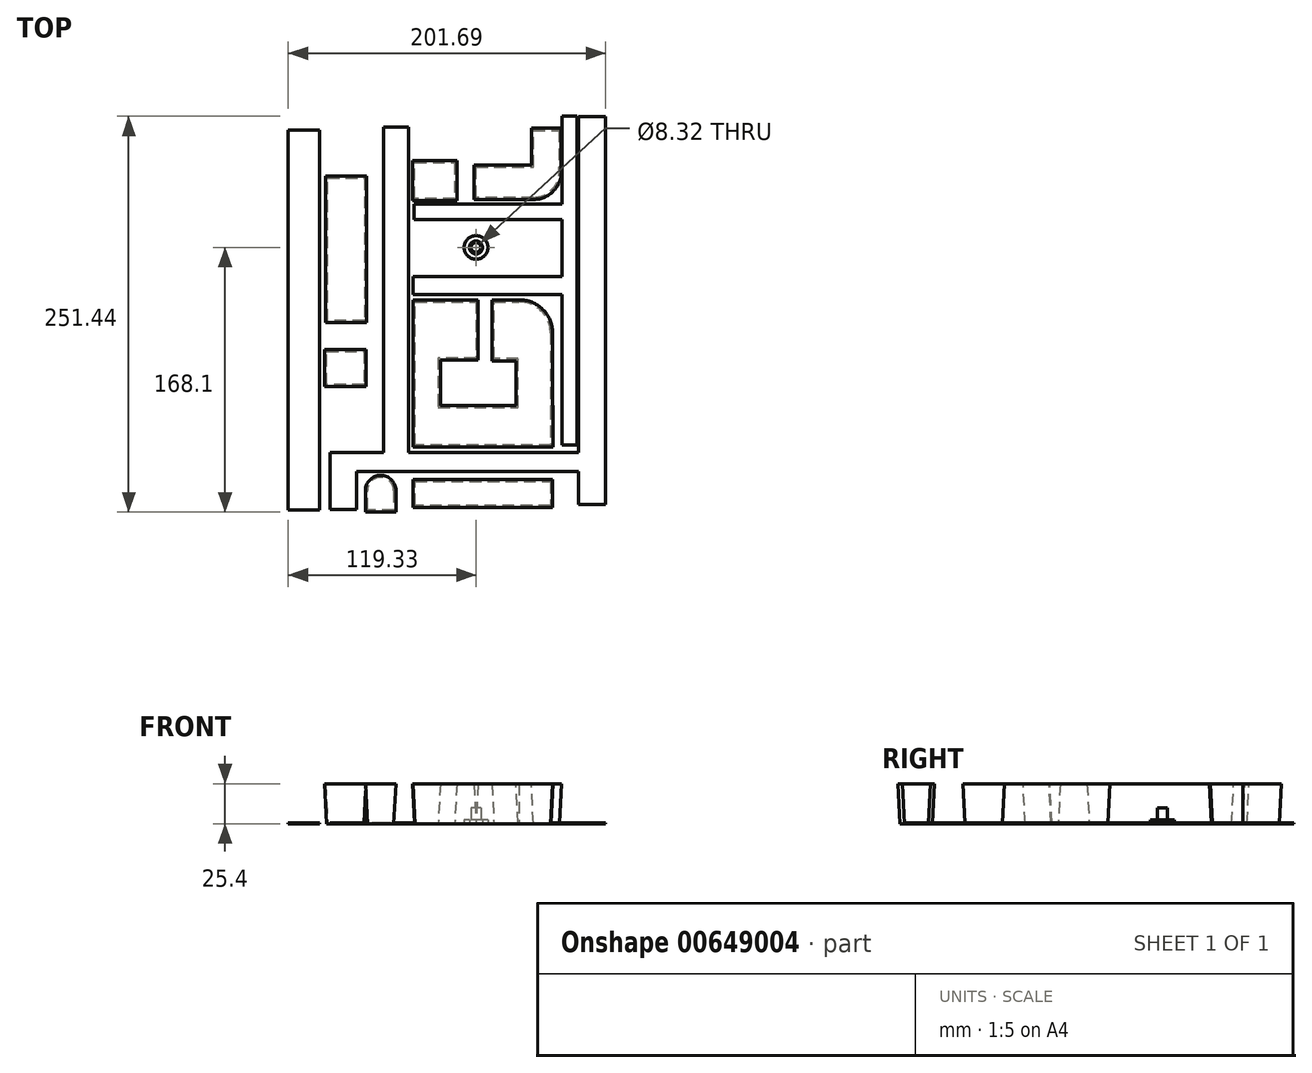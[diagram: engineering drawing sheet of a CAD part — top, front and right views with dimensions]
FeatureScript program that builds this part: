
annotation { "Feature Type Name" : "Feature", "Feature Type Description" : "" }
export const myFeature = defineFeature(function(context is Context, id is Id, definition is map)
    precondition{}
    {
        {
            var Q0;
            Q0=qCreatedBy(makeId("Top.planeOp"),FACE);
            var sketch = newSketch(context, id + "F0", { "sketchPlane" : qUnion([Q0])});
            skLineSegment(sketch, "E0.bottom", {"start": v(-38.9, 53.75) * mm, "end": v(-13.5, 53.75) * mm});
            skLineSegment(sketch, "E0.top", {"start": v(-38.9, 31.17) * mm, "end": v(-13.5, 31.17) * mm});
            skLineSegment(sketch, "E0.left", {"start": v(-38.9, 53.75) * mm, "end": v(-38.9, 31.17) * mm});
            skLineSegment(sketch, "E0.right", {"start": v(-13.5, 53.75) * mm, "end": v(-13.5, 31.17) * mm});
            skLineSegment(sketch, "E1.bottom", {"start": v(36.45, 51.05) * mm, "end": v(52.67, 51.05) * mm});
            skLineSegment(sketch, "E1.top", {"start": v(36.45, 74.37) * mm, "end": v(52.67, 74.37) * mm});
            skLineSegment(sketch, "E1.left", {"start": v(36.45, 51.05) * mm, "end": v(36.45, 74.37) * mm});
            skLineSegment(sketch, "E1.right", {"start": v(52.67, 51.05) * mm, "end": v(52.67, 74.37) * mm});
            skLineSegment(sketch, "E2.bottom", {"start": v(-70.95, 43.93) * mm, "end": v(-94.3, 43.93) * mm});
            skLineSegment(sketch, "E2.top", {"start": v(-70.95, -46.47) * mm, "end": v(-94.3, -46.47) * mm});
            skLineSegment(sketch, "E2.left", {"start": v(-70.95, 43.93) * mm, "end": v(-70.95, -46.47) * mm});
            skLineSegment(sketch, "E2.right", {"start": v(-94.3, 43.93) * mm, "end": v(-94.3, -46.47) * mm});
            skLineSegment(sketch, "E3.bottom", {"start": v(-38.66, -34.6) * mm, "end": v(0, -34.6) * mm});
            skLineSegment(sketch, "E3.top", {"start": v(-38.66, -70.2) * mm, "end": v(0, -70.2) * mm});
            skLineSegment(sketch, "E3.left", {"start": v(-38.66, -34.6) * mm, "end": v(-38.66, -70.2) * mm});
            skLineSegment(sketch, "E3.right", {"start": v(0, -34.6) * mm, "end": v(0, -70.2) * mm});
            skLineSegment(sketch, "E4.bottom", {"start": v(27.37, -34.6) * mm, "end": v(11.41, -34.6) * mm});
            skLineSegment(sketch, "E4.top", {"start": v(27.37, -70.68) * mm, "end": v(11.41, -70.68) * mm});
            skLineSegment(sketch, "E4.left", {"start": v(27.37, -34.6) * mm, "end": v(27.37, -70.68) * mm});
            skLineSegment(sketch, "E4.right", {"start": v(11.41, -34.6) * mm, "end": v(11.41, -70.68) * mm});
            skLineSegment(sketch, "E5.bottom", {"start": v(27.37, -70.68) * mm, "end": v(47.25, -70.68) * mm});
            skLineSegment(sketch, "E5.top", {"start": v(27.37, -54.24) * mm, "end": v(47.25, -54.24) * mm});
            skLineSegment(sketch, "E5.left", {"start": v(27.37, -70.68) * mm, "end": v(27.37, -54.24) * mm});
            skLineSegment(sketch, "E5.right", {"start": v(47.25, -70.68) * mm, "end": v(47.25, -54.24) * mm});
            skArc(sketch, "E6", {"start": v(47.25, -54.24) * mm, "mid": v(41.4, -40.27) * mm, "end": v(27.37, -34.6) * mm});
            skLineSegment(sketch, "E7.bottom", {"start": v(36.45, 51.05) * mm, "end": v(0, 51.05) * mm});
            skLineSegment(sketch, "E7.top", {"start": v(36.45, 31.78) * mm, "end": v(0, 31.78) * mm});
            skLineSegment(sketch, "E7.left", {"start": v(36.45, 51.05) * mm, "end": v(36.45, 31.78) * mm});
            skLineSegment(sketch, "E7.right", {"start": v(0, 51.05) * mm, "end": v(0, 31.78) * mm});
            skArc(sketch, "E8", {"start": v(36.45, 31.78) * mm, "mid": v(49.04, 37.64) * mm, "end": v(52.67, 51.05) * mm});
            skLineSegment(sketch, "E9.bottom", {"start": v(-38.66, -70.2) * mm, "end": v(-23.99, -70.2) * mm});
            skLineSegment(sketch, "E9.top", {"start": v(-38.66, -125.52) * mm, "end": v(-23.99, -125.52) * mm});
            skLineSegment(sketch, "E9.left", {"start": v(-38.66, -70.2) * mm, "end": v(-38.66, -125.52) * mm});
            skLineSegment(sketch, "E9.right", {"start": v(-23.99, -70.2) * mm, "end": v(-23.99, -125.52) * mm});
            skLineSegment(sketch, "E10.bottom", {"start": v(-23.99, -125.52) * mm, "end": v(47.47, -125.52) * mm});
            skLineSegment(sketch, "E10.top", {"start": v(-23.99, -101.65) * mm, "end": v(47.47, -101.65) * mm});
            skLineSegment(sketch, "E10.left", {"start": v(-23.99, -125.52) * mm, "end": v(-23.99, -101.65) * mm});
            skLineSegment(sketch, "E10.right", {"start": v(47.47, -125.52) * mm, "end": v(47.47, -101.65) * mm});
            skLineSegment(sketch, "E11.bottom", {"start": v(47.25, -70.68) * mm, "end": v(26.75, -70.68) * mm});
            skLineSegment(sketch, "E11.top", {"start": v(47.25, -101.65) * mm, "end": v(26.75, -101.65) * mm});
            skLineSegment(sketch, "E11.left", {"start": v(47.25, -70.68) * mm, "end": v(47.25, -101.65) * mm});
            skLineSegment(sketch, "E11.right", {"start": v(26.75, -70.68) * mm, "end": v(26.75, -101.65) * mm});
            skLineSegment(sketch, "E12.bottom", {"start": v(-38.66, -148.73) * mm, "end": v(47.25, -148.73) * mm});
            skLineSegment(sketch, "E12.top", {"start": v(-38.66, -163.92) * mm, "end": v(47.25, -163.92) * mm});
            skLineSegment(sketch, "E12.left", {"start": v(-38.66, -148.73) * mm, "end": v(-38.66, -163.92) * mm});
            skLineSegment(sketch, "E12.right", {"start": v(47.25, -148.73) * mm, "end": v(47.25, -163.92) * mm});
            skLineSegment(sketch, "E13.bottom", {"start": v(-52.23, -154.48) * mm, "end": v(-68.96, -154.48) * mm});
            skLineSegment(sketch, "E13.top", {"start": v(-52.23, -166.77) * mm, "end": v(-68.96, -166.77) * mm});
            skLineSegment(sketch, "E13.left", {"start": v(-52.23, -154.48) * mm, "end": v(-52.23, -166.77) * mm});
            skLineSegment(sketch, "E13.right", {"start": v(-68.96, -154.48) * mm, "end": v(-68.96, -166.77) * mm});
            skArc(sketch, "E14", {"start": v(-52.23, -154.48) * mm, "mid": v(-60.6, -146.12) * mm, "end": v(-68.96, -154.48) * mm});
            skLineSegment(sketch, "E15.bottom", {"start": v(-71.15, -87.16) * mm, "end": v(-94.82, -87.16) * mm});
            skLineSegment(sketch, "E15.top", {"start": v(-71.15, -66.22) * mm, "end": v(-94.82, -66.22) * mm});
            skLineSegment(sketch, "E15.left", {"start": v(-71.15, -87.16) * mm, "end": v(-71.15, -66.22) * mm});
            skLineSegment(sketch, "E15.right", {"start": v(-94.82, -87.16) * mm, "end": v(-94.82, -66.22) * mm});
            skSolve(sketch);
        }
        {
            var Q0;
            Q0 = qSketchRegion(id + "F0", true);
            extrude(context, id + "F1", {"entities" : qUnion([Q0]), "depth" : 25.4 * mm, "offsetDistance" : 25.4 * mm, "hasDraft" : true, "draftAngle" : 3 * degree});
        }
        {
            var Q0;
            Q0=qCreatedBy(makeId("Top.planeOp"),FACE);
            var sketch = newSketch(context, id + "F2", { "sketchPlane" : qUnion([Q0])});
            skLineSegment(sketch, "E16.bottom", {"start": v(-42.79, -130.3) * mm, "end": v(-58.6, -130.3) * mm});
            skLineSegment(sketch, "E16.top", {"start": v(-42.79, 76.57) * mm, "end": v(-58.6, 76.57) * mm});
            skLineSegment(sketch, "E16.left", {"start": v(-42.79, -130.3) * mm, "end": v(-42.79, 76.57) * mm});
            skLineSegment(sketch, "E16.right", {"start": v(-58.6, -130.3) * mm, "end": v(-58.6, 76.57) * mm});
            skLineSegment(sketch, "E17.bottom", {"start": v(-99.38, -166.7) * mm, "end": v(-119.33, -166.7) * mm});
            skLineSegment(sketch, "E17.top", {"start": v(-99.38, 74.63) * mm, "end": v(-119.33, 74.63) * mm});
            skLineSegment(sketch, "E17.left", {"start": v(-99.38, -166.7) * mm, "end": v(-99.38, 74.63) * mm});
            skLineSegment(sketch, "E17.right", {"start": v(-119.33, -166.7) * mm, "end": v(-119.33, 74.63) * mm});
            skLineSegment(sketch, "E18.bottom", {"start": v(-42.79, -130.3) * mm, "end": v(65.06, -130.3) * mm});
            skLineSegment(sketch, "E18.top", {"start": v(-75.89, -142.36) * mm, "end": v(65.06, -142.36) * mm});
            skLineSegment(sketch, "E18.right", {"start": v(65.06, -130.3) * mm, "end": v(65.06, -142.36) * mm});
            skLineSegment(sketch, "E19.bottom", {"start": v(-75.89, -166.46) * mm, "end": v(-92.66, -166.46) * mm});
            skLineSegment(sketch, "E19.top", {"start": v(-75.89, -142.36) * mm, "end": v(-92.66, -142.36) * mm});
            skLineSegment(sketch, "E19.left", {"start": v(-75.89, -166.46) * mm, "end": v(-75.89, -142.36) * mm});
            skLineSegment(sketch, "E19.right", {"start": v(-92.66, -166.46) * mm, "end": v(-92.66, -142.36) * mm});
            skLineSegment(sketch, "E20.bottom", {"start": v(82.36, -163.32) * mm, "end": v(65.06, -163.32) * mm});
            skLineSegment(sketch, "E20.top", {"start": v(82.36, 82.96) * mm, "end": v(65.06, 82.96) * mm});
            skLineSegment(sketch, "E20.left", {"start": v(82.36, -163.32) * mm, "end": v(82.36, 82.96) * mm});
            skLineSegment(sketch, "E20.right", {"start": v(65.06, -163.32) * mm, "end": v(65.06, 82.96) * mm});
            skLineSegment(sketch, "E21.bottom", {"start": v(-58.6, -130.3) * mm, "end": v(-92.66, -130.3) * mm});
            skLineSegment(sketch, "E21.top", {"start": v(-58.6, -142.36) * mm, "end": v(-92.66, -142.36) * mm});
            skLineSegment(sketch, "E21.left", {"start": v(-58.6, -130.3) * mm, "end": v(-58.6, -142.36) * mm});
            skLineSegment(sketch, "E21.right", {"start": v(-92.66, -130.3) * mm, "end": v(-92.66, -142.36) * mm});
            skSolve(sketch);
        }
        {
            var Q0;
            Q0 = qSketchRegion(id + "F2", true);
            extrude(context, id + "F3", {"entities" : qUnion([Q0]), "depth" : 0.5 * mm, "offsetDistance" : 25.4 * mm});
        }
        {
            var Q0;
            Q0=qCreatedBy(makeId("Top.planeOp"),FACE);
            var sketch = newSketch(context, id + "F4", { "sketchPlane" : qUnion([Q0])});
            skCircle(sketch, "E22", {"center": v(0, 0) * mm, "radius": 4.16 * mm});
            skCircle(sketch, "E23", {"center": v(0, 0) * mm, "radius": 7.53 * mm});
            skSolve(sketch);
        }
        {
            var Q0;
            Q0=qCreatedBy(makeId("Top.planeOp"),FACE);
            var sketch = newSketch(context, id + "F5", { "sketchPlane" : qUnion([Q0])});
            skCircle(sketch, "E24", {"center": v(0, 0) * mm, "radius": 3.07 * mm});
            skSolve(sketch);
        }
        {
            var Q0;
            Q0 = qSketchRegion(id + "F4", true);
            extrude(context, id + "F6", {"entities" : qUnion([Q0]), "depth" : 2.54 * mm, "offsetDistance" : 25.4 * mm});
        }
        {
            var Q0;
            Q0 = qSketchRegion(id + "F5", true);
            extrude(context, id + "F7", {"entities" : qUnion([Q0]), "depth" : 10.16 * mm, "offsetDistance" : 25.4 * mm});
        }
        {
            var Q0;
            Q0=qCreatedBy(makeId("Top.planeOp"),FACE);
            var sketch = newSketch(context, id + "F8", { "sketchPlane" : qUnion([Q0])});
            skLineSegment(sketch, "E25.bottom", {"start": v(-39.3, 27.7) * mm, "end": v(59.9, 27.7) * mm});
            skLineSegment(sketch, "E25.top", {"start": v(-39.3, 17.73) * mm, "end": v(59.9, 17.73) * mm});
            skLineSegment(sketch, "E25.left", {"start": v(-39.3, 27.7) * mm, "end": v(-39.3, 17.73) * mm});
            skLineSegment(sketch, "E25.right", {"start": v(59.9, 27.7) * mm, "end": v(59.9, 17.73) * mm});
            skLineSegment(sketch, "E26.bottom", {"start": v(-39.83, -30.05) * mm, "end": v(59.9, -30.05) * mm});
            skLineSegment(sketch, "E26.top", {"start": v(-39.83, -18.5) * mm, "end": v(59.9, -18.5) * mm});
            skLineSegment(sketch, "E26.left", {"start": v(-39.83, -30.05) * mm, "end": v(-39.83, -18.5) * mm});
            skLineSegment(sketch, "E26.right", {"start": v(59.9, -30.05) * mm, "end": v(59.9, -18.5) * mm});
            skLineSegment(sketch, "E27.bottom", {"start": v(54.66, 83.34) * mm, "end": v(64.1, 83.34) * mm});
            skLineSegment(sketch, "E27.top", {"start": v(54.66, -125.59) * mm, "end": v(64.1, -125.59) * mm});
            skLineSegment(sketch, "E27.left", {"start": v(54.66, 83.34) * mm, "end": v(54.66, -125.59) * mm});
            skLineSegment(sketch, "E27.right", {"start": v(64.1, 83.34) * mm, "end": v(64.1, -125.59) * mm});
            skSolve(sketch);
        }
        {
            var Q0;
            Q0 = qSketchRegion(id + "F8", true);
            extrude(context, id + "F9", {"entities" : qUnion([Q0]), "depth" : 0.5 * mm, "offsetDistance" : 25.4 * mm});
        }
    });
